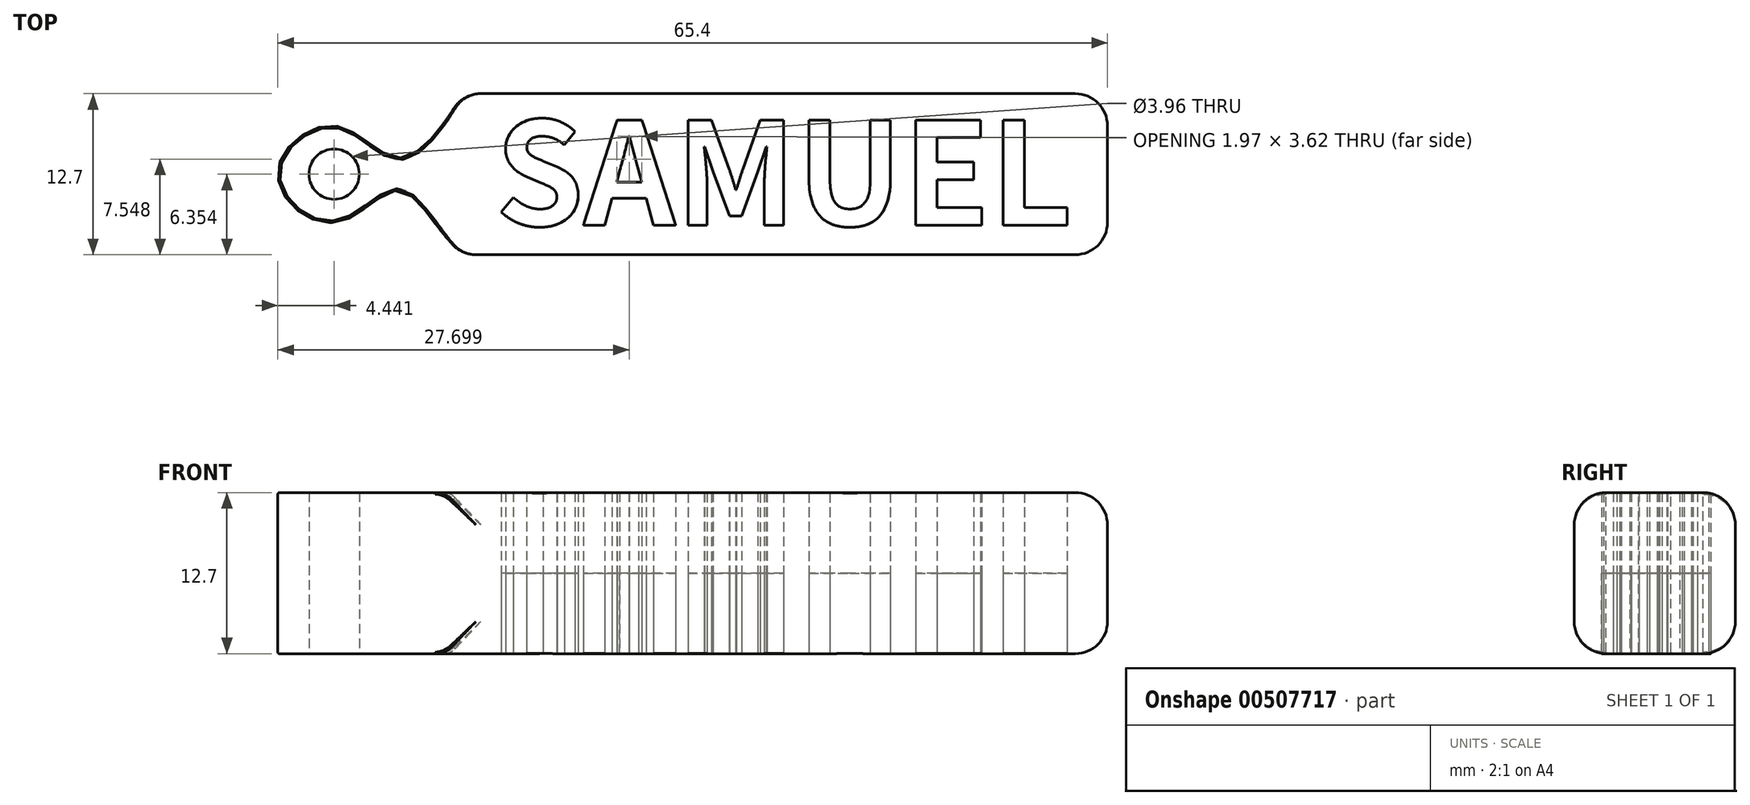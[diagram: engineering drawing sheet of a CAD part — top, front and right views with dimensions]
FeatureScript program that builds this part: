
annotation { "Feature Type Name" : "Feature", "Feature Type Description" : "" }
export const myFeature = defineFeature(function(context is Context, id is Id, definition is map)
    precondition{}
    {
        {
            var Q0;
            Q0=qCreatedBy(makeId("Top.planeOp"),FACE);
            var sketch = newSketch(context, id + "F0", { "sketchPlane" : qUnion([Q0])});
            skLineSegment(sketch, "E0.bottom", {"start": v(-26.13, 8.6) * mm, "end": v(22.13, 8.6) * mm});
            skLineSegment(sketch, "E0.top", {"start": v(-26.13, -4.1) * mm, "end": v(22.13, -4.1) * mm});
            skLineSegment(sketch, "E0.left", {"start": v(-26.13, 8.6) * mm, "end": v(-26.13, -4.1) * mm});
            skLineSegment(sketch, "E0.right", {"start": v(24.67, 6.06) * mm, "end": v(24.67, -1.56) * mm});
            skText(sketch, "E1", { "text": "SAMUEL", "fontName": "NotoSansCJKjp-Bold.otf"});
            skFitSpline(sketch, "E2", {"points": [v(-26.13, -4.1) * mm, v(-31.2, 0.98) * mm, v(-36.29, -1.56) * mm, v(-40.73, 2.25) * mm, v(-36.29, 6.06) * mm, v(-31.2, 3.52) * mm, v(-26.13, 8.6) * mm], "startDerivative": vector(-35.18, 29.5) * mm, "endDerivative": vector(24.4, 40.03) * mm});
            skCircle(sketch, "E3", {"center": v(-36.29, 2.25) * mm, "radius": 1.98 * mm});
            skPoint(sketch, "E4.visualSharp", {"position": v(24.67, 8.6) * mm});
            skArc(sketch, "E4.filletArc", {"start": v(24.67, 6.06) * mm, "mid": v(23.93, 7.86) * mm, "end": v(22.13, 8.6) * mm});
            skPoint(sketch, "E5.visualSharp", {"position": v(24.67, -4.1) * mm});
            skArc(sketch, "E5.filletArc", {"start": v(22.13, -4.1) * mm, "mid": v(23.93, -3.35) * mm, "end": v(24.67, -1.56) * mm});
            const initialGuessF0  = {"E1": [-0.02359, -0.00178, 1, 0, 0.00807]};
            skSetInitialGuess(sketch, initialGuessF0);
            skSolve(sketch);
        }
        {
            var Q0;
            Q0=makeQuery(id+"F0.imprint","IMPRINT",FACE,{"disambiguationData":[TD([[makeQuery(id+"F0.imprint","IMPRINT",EDGE,{"derivedFrom":sQuery(id+"F0.wireOp",EDGE,"E0.bottom")}),-1.0]])]});
            var Q1;
            Q1=makeQuery(id+"F0.imprint","IMPRINT",FACE,{"disambiguationData":[TD([[makeQuery(id+"F0.imprint","IMPRINT",EDGE,{"derivedFrom":sQuery(id+"F0.wireOp",EDGE,"E1.sketch_text.stroke-16")}),-1.0]])]});
            extrude(context, id + "F1", {"entities" : qUnion([Q0, Q1]), "depth" : 12.7 * mm});
        }
        {
            var Q0;
            Q0=makeQuery(id+"F0.imprint","IMPRINT",FACE,{"disambiguationData":[TD([[makeQuery(id+"F0.imprint","IMPRINT",EDGE,{"derivedFrom":sQuery(id+"F0.wireOp",EDGE,"E1.sketch_text.stroke-16")}),1.0]])]});
            var Q1;
            Q1=makeQuery(id+"F0.imprint","IMPRINT",FACE,{"disambiguationData":[TD([[makeQuery(id+"F0.imprint","IMPRINT",EDGE,{"derivedFrom":sQuery(id+"F0.wireOp",EDGE,"E1.sketch_text.stroke-0")}),1.0]])]});
            var Q2;
            Q2=makeQuery(id+"F0.imprint","IMPRINT",FACE,{"disambiguationData":[TD([[makeQuery(id+"F0.imprint","IMPRINT",EDGE,{"derivedFrom":sQuery(id+"F0.wireOp",EDGE,"E1.sketch_text.stroke-30")}),1.0]])]});
            var Q3;
            Q3=makeQuery(id+"F0.imprint","IMPRINT",FACE,{"disambiguationData":[TD([[makeQuery(id+"F0.imprint","IMPRINT",EDGE,{"derivedFrom":sQuery(id+"F0.wireOp",EDGE,"E1.sketch_text.stroke-52")}),1.0]])]});
            var Q4;
            Q4=makeQuery(id+"F0.imprint","IMPRINT",FACE,{"disambiguationData":[TD([[makeQuery(id+"F0.imprint","IMPRINT",EDGE,{"derivedFrom":sQuery(id+"F0.wireOp",EDGE,"E1.sketch_text.stroke-62")}),1.0]])]});
            var Q5;
            Q5=makeQuery(id+"F0.imprint","IMPRINT",FACE,{"disambiguationData":[TD([[makeQuery(id+"F0.imprint","IMPRINT",EDGE,{"derivedFrom":sQuery(id+"F0.wireOp",EDGE,"E1.sketch_text.stroke-74")}),1.0]])]});
            extrude(context, id + "F2", {"entities" : qUnion([Q0, Q1, Q2, Q3, Q4, Q5]), "depth" : 6.35 * mm});
        }
        {
            var Q0;
            Q0=makeQuery(id+"F0.imprint","IMPRINT",FACE,{"disambiguationData":[TD([[makeQuery(id+"F0.imprint","IMPRINT",EDGE,{"derivedFrom":sQuery(id+"F0.wireOp",EDGE,"E0.left")}),-1.0]])]});
            extrude(context, id + "F3", {"entities" : qUnion([Q0]), "operationType" : NewBodyOperationType.ADD, "depth" : 12.7 * mm});
        }
        {
            var Q0;
            Q0=makeQuery(id+"F1.opExtrude","CAP_EDGE",EDGE,{"disambiguationData":[OSD([sQuery(id+"F0.wireOp",EDGE,"E0.bottom")])],"isStart":true});
            var Q1;
            Q1=makeQuery(id+"F1.opExtrude","CAP_EDGE",EDGE,{"disambiguationData":[OSD([sQuery(id+"F0.wireOp",EDGE,"E0.bottom")])],"isStart":false});
            var Q2;
            Q2=makeQuery(id+"F1.opExtrude","CAP_EDGE",EDGE,{"disambiguationData":[OSD([sQuery(id+"F0.wireOp",EDGE,"E0.top")])],"isStart":false});
            var Q3;
            {var subQ0=sQuery(id+"F0.wireOp",EDGE,"E2");var subQ1=sQuery(id+"F0.wireOp",EDGE,"E0.left");var subQ2=sQuery(id+"F0.wireOp",EDGE,"E0.bottom");Q3=makeQuery(id+"F3.boolean.opBoolean","MERGE",EDGE,{"derivedFrom":[makeQuery(id+"F1.opExtrude","SWEPT_EDGE",EDGE,{"disambiguationData":[OSD([subQ2,subQ1,subQ0])]}),makeQuery(id+"F3.opExtrude","SWEPT_EDGE",EDGE,{"disambiguationData":[OSD([subQ2,subQ1,subQ0])]})]});}
            var Q4;
            {var subQ0=sQuery(id+"F0.wireOp",EDGE,"E2");var subQ1=sQuery(id+"F0.wireOp",EDGE,"E0.left");var subQ2=sQuery(id+"F0.wireOp",EDGE,"E0.top");Q4=makeQuery(id+"F3.boolean.opBoolean","MERGE",EDGE,{"derivedFrom":[makeQuery(id+"F1.opExtrude","SWEPT_EDGE",EDGE,{"disambiguationData":[OSD([subQ2,subQ1,subQ0])]}),makeQuery(id+"F3.opExtrude","SWEPT_EDGE",EDGE,{"disambiguationData":[OSD([subQ2,subQ1,subQ0])]})]});}
            fillet(context, id + "F4", {"entities" : qUnion([Q0, Q1, Q2, Q3, Q4]), "radius" : 2.54 * mm, "tangentPropagation" : true, "allowEdgeOverflow" : false});
        }
        {
            var Q0;
            Q0=makeQuery(id+"F3.opExtrude","CAP_EDGE",EDGE,{"disambiguationData":[OSD([sQuery(id+"F0.wireOp",EDGE,"E2")])],"isStart":false});
            var Q1;
            Q1=makeQuery(id+"F3.opExtrude","CAP_EDGE",EDGE,{"disambiguationData":[OSD([sQuery(id+"F0.wireOp",EDGE,"E2")])],"isStart":true});
            fillet(context, id + "F5", {"entities" : qUnion([Q0, Q1]), "radius" : 0.13 * mm, "tangentPropagation" : true, "allowEdgeOverflow" : false});
        }
    });
